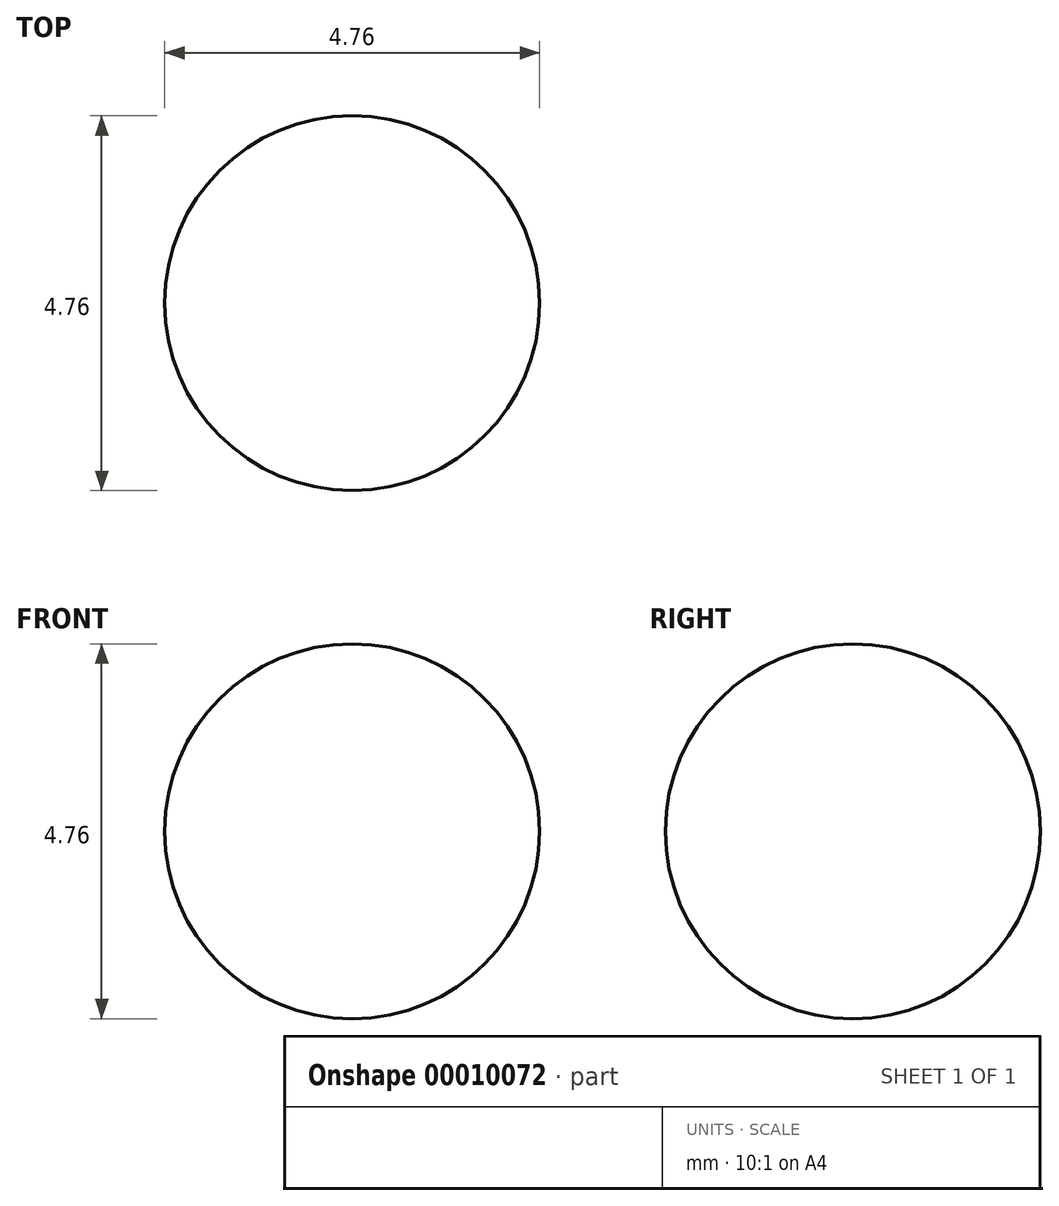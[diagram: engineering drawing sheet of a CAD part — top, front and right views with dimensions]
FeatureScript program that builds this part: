
annotation { "Feature Type Name" : "Feature", "Feature Type Description" : "" }
export const myFeature = defineFeature(function(context is Context, id is Id, definition is map)
    precondition{}
    {
        {
            var Q0;
            Q0=qCreatedBy(makeId("Right.planeOp"),FACE);
            var sketch = newSketch(context, id + "F0", { "sketchPlane" : qUnion([Q0])});
            skArc(sketch, "E0", {"start": v(0, -2.38) * mm, "mid": v(2.38, 0) * mm, "end": v(0, 2.38) * mm});
            skLineSegment(sketch, "E1", {"start": v(0, 2.38) * mm, "end": v(0, -2.38) * mm});
            skSolve(sketch);
        }
        {
            var Q0;
            Q0=makeQuery(id+"F0.imprint","IMPRINT",FACE,{"disambiguationData":[TD([[makeQuery(id+"F0.imprint","IMPRINT",EDGE,{"derivedFrom":sQuery(id+"F0.wireOp",EDGE,"E0")}),1.0]])]});
            var Q1;
            Q1=sQuery(id+"F0.wireOp",EDGE,"E1");
            revolve(context, id + "F1", {"entities" : qUnion([Q0]), "axis" : qUnion([Q1]), "revolveType" : RevolveType.FULL});
        }
    });
